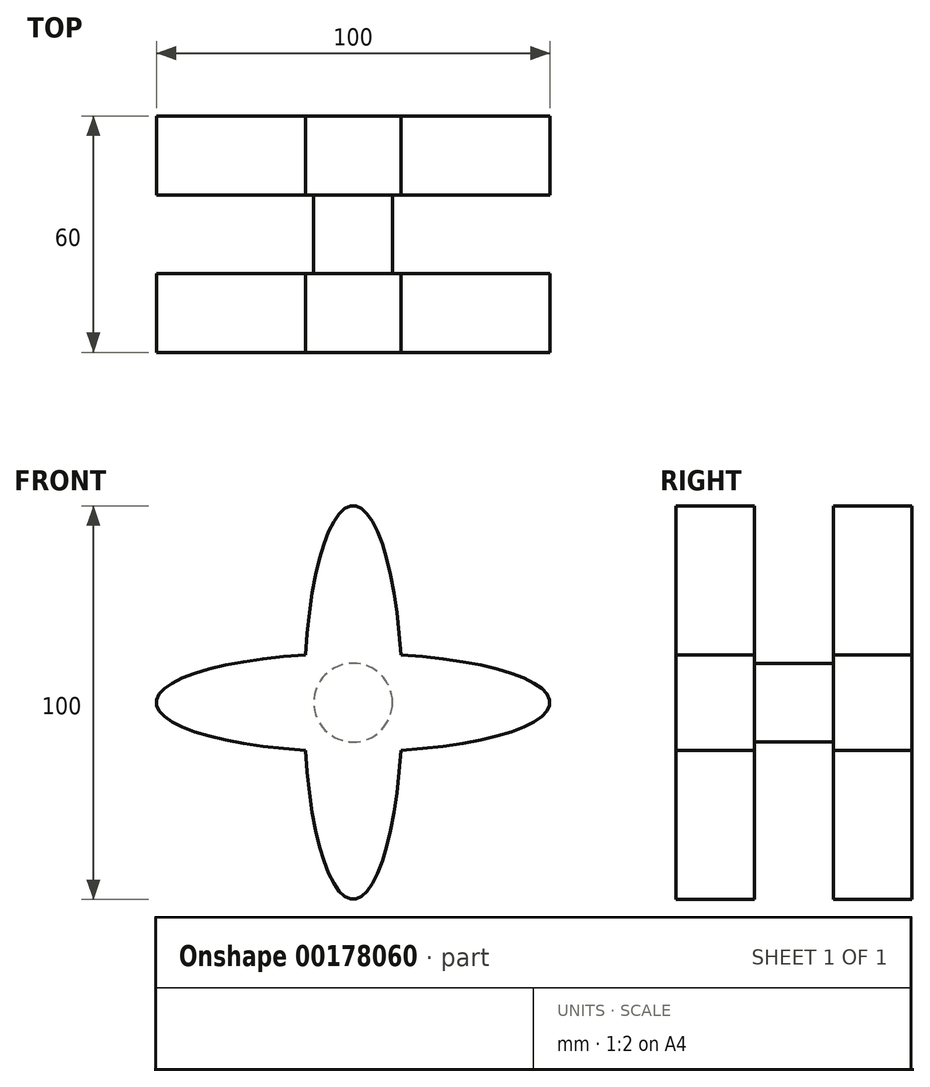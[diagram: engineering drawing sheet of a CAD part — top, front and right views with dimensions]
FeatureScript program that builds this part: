
annotation { "Feature Type Name" : "Feature", "Feature Type Description" : "" }
export const myFeature = defineFeature(function(context is Context, id is Id, definition is map)
    precondition{}
    {
        {
            var Q0;
            Q0=qCreatedBy(makeId("Front.planeOp"),FACE);
            var sketch = newSketch(context, id + "F0", { "sketchPlane" : qUnion([Q0])});
            skEllipse(sketch, "E0", {"center": v(0, 0) * mm, "majorRadius": 50 * mm, "minorRadius": 12.5 * mm, "majorAxis": v(0, 1)});
            skEllipse(sketch, "E1", {"center": v(0, 0) * mm, "majorRadius": 50 * mm, "minorRadius": 12.5 * mm, "majorAxis": v(1, 0)});
            skSolve(sketch);
        }
        {
            var Q0;
            Q0=qSketchRegion(id+"F0",true);
            extrude(context, id + "F1", {"entities" : qUnion([Q0]), "depth" : 20 * mm});
        }
        {
            var Q0;
            Q0=makeQuery(id+"F1.opExtrude","CAP_FACE",FACE,{"disambiguationData":[OSD([sQuery(id+"F0.wireOp",EDGE,"E0"),sQuery(id+"F0.wireOp",EDGE,"E1")])],"isStart":true});
            var sketch = newSketch(context, id + "F2", { "sketchPlane" : qUnion([Q0])});
            skCircle(sketch, "E2", {"center": v(0, 0) * mm, "radius": 10 * mm});
            skSolve(sketch);
        }
        {
            var Q0;
            Q0 = qSketchRegion(id + "F2", true);
            extrude(context, id + "F3", {"entities" : qUnion([Q0]), "operationType" : NewBodyOperationType.ADD, "depth" : 20 * mm});
        }
        {
            var Q0;
            Q0=makeQuery(id+"F3.opExtrude","CAP_FACE",FACE,{"disambiguationData":[OSD([sQuery(id+"F2.wireOp",EDGE,"E2")])],"isStart":false});
            var sketch = newSketch(context, id + "F4", { "sketchPlane" : qUnion([Q0])});
            skEllipse(sketch, "E3", {"center": v(0, 0) * mm, "majorRadius": 50 * mm, "minorRadius": 12.5 * mm, "majorAxis": v(0, 1)});
            skEllipse(sketch, "E4", {"center": v(0, 0) * mm, "majorRadius": 50 * mm, "minorRadius": 12.5 * mm, "majorAxis": v(1, 0)});
            skSolve(sketch);
        }
        {
            var Q0;
            Q0 = qSketchRegion(id + "F4", true);
            extrude(context, id + "F5", {"entities" : qUnion([Q0]), "operationType" : NewBodyOperationType.ADD, "depth" : 20 * mm});
        }
    });
